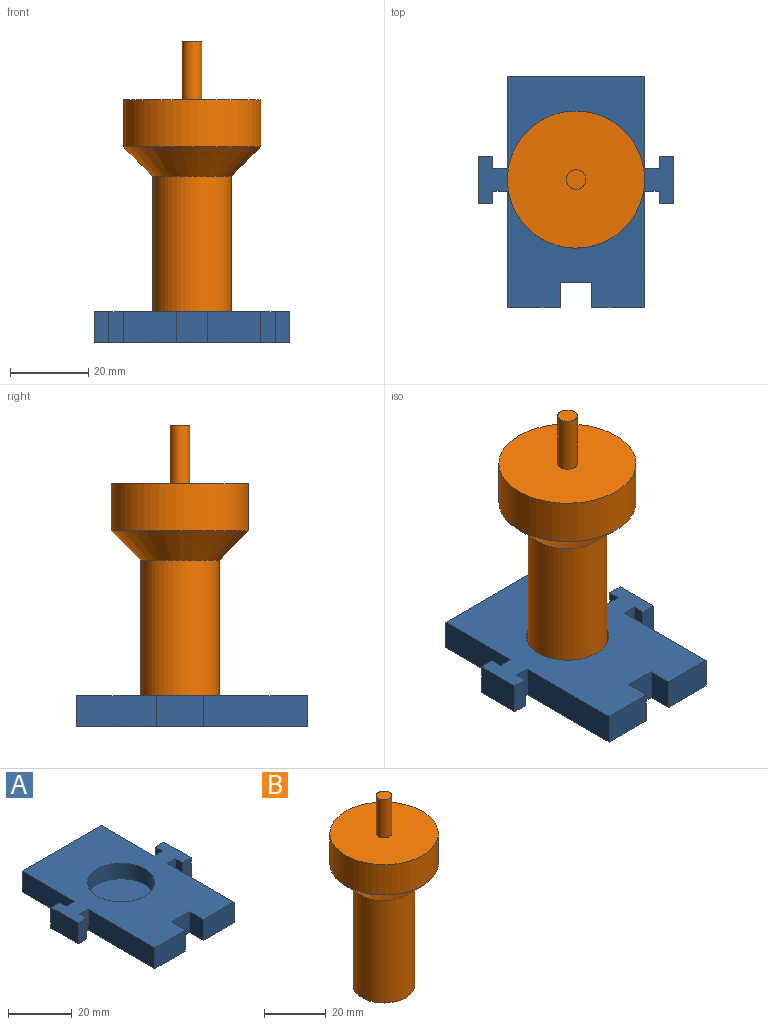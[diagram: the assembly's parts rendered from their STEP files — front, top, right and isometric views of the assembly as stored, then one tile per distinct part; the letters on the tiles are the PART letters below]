
ASSEMBLY  parts=2 mates=1
PART A: 28 faces, bbox 50x58.8x8 mm
  f0: plane 13.49x8mm, normal (0,-1,0), area 107.9mm2, adj f1,f24,f25,f26
  f1: plane 29.57x8mm, normal (1,0,0), area 236.5mm2, adj f0,f2,f25,f26
  f2: plane 8x3.73mm, normal (0,-1,0), area 29.8mm2, adj f1,f3,f25,f26
  f3: plane 8x3.08mm, normal (-1,0,0), area 24.7mm2, adj f2,f4,f25,f26
  f4: plane 8x3.77mm, normal (0,-1,0), area 30.1mm2, adj f3,f5,f25,f26
  f5: plane 12.03x8mm, normal (1,0,0), area 96.3mm2, adj f4,f6,f25,f26
  f6: plane 8x3.77mm, normal (0,1,0), area 30.1mm2, adj f5,f7,f25,f26
  f7: plane 8x3.08mm, normal (-1,0,0), area 24.7mm2, adj f6,f8,f25,f26
  f8: plane 8x3.73mm, normal (0,1,0), area 29.8mm2, adj f7,f9,f25,f26
  f9: plane 23.41x8mm, normal (1,0,0), area 187.3mm2, adj f8,f10,f25,f26
  f10: plane 35x8mm, normal (0,1,0), area 280mm2, adj f9,f11,f25,f26
  f11: plane 23.41x8mm, normal (-1,0,0), area 187.3mm2, adj f10,f12,f25,f26
  f12: plane 8x3.73mm, normal (0,1,0), area 29.8mm2, adj f11,f13,f25,f26
  f13: plane 8x3.08mm, normal (1,0,0), area 24.7mm2, adj f12,f14,f25,f26
  f14: plane 8x3.77mm, normal (0,1,0), area 30.1mm2, adj f13,f15,f25,f26
  f15: plane 12.03x8mm, normal (-1,0,0), area 96.3mm2, adj f14,f16,f25,f26
  f16: plane 8x3.77mm, normal (0,-1,0), area 30.1mm2, adj f15,f17,f25,f26
  f17: plane 8x3.08mm, normal (1,0,0), area 24.7mm2, adj f16,f18,f25,f26
  f18: plane 8x3.73mm, normal (0,-1,0), area 29.8mm2, adj f17,f19,f25,f26
  f19: plane 29.57x8mm, normal (-1,0,0), area 236.5mm2, adj f18,f20,f25,f26
  f20: plane 13.49x8mm, normal (0,-1,0), area 107.9mm2, adj f19,f21,f25,f26
  f21: plane 8x6.35mm, normal (1,0,0), area 50.8mm2, adj f20,f22,f25,f26
  f22: plane 8.02x8mm, normal (0,-1,0), area 64.2mm2, adj f21,f24,f25,f26
  f23: cylinder r=10.5mm len=21mm, axis (0,0,-1), area 395.8mm2, adj f25,f27
  f24: plane 8x6.35mm, normal (-1,0,0), area 50.8mm2, adj f0,f22,f25,f26
  f25: plane 58.84x50mm, normal (0,0,1), area 1796.6mm2, adj f0,f1,f2,f3,f4,f5,f6,f7
  f26: plane 58.84x50mm, normal (0,0,-1), area 2142.9mm2, adj f0,f1,f2,f3,f4,f5,f6,f7
  f27: plane 21x21mm, normal (0,0,1), area 346.4mm2, adj f23
PART B: 7 faces, bbox 35x35x75 mm
  f0: cylinder r=17.5mm len=35mm, axis (0,0,-1), area 1319.5mm2, adj f1,f5
  f1: plane 35x35mm, normal (0,0,1), area 942.5mm2, adj f0,f3
  f2: cylinder r=10mm len=40.5mm, axis (0,0,-1), area 2544.7mm2, adj f5,f6
  f3: cylinder r=2.5mm len=15mm, axis (0,0,-1), area 235.6mm2, adj f1,f4
  f4: plane 5x5mm, normal (0,0,1), area 19.6mm2, adj f3
  f5: cone r=17.5mm half-angle=45deg, axis (0,0,1), area 916.3mm2, adj f0,f2
  f6: plane 20x20mm, normal (0,0,-1), area 314.2mm2, adj f2
PLACE A at identity
PLACE B t=(0,50,22)mm
MATE fastened B.f2 <-> A.f23  axis (0,0,-1) through (0,50,2)mm
